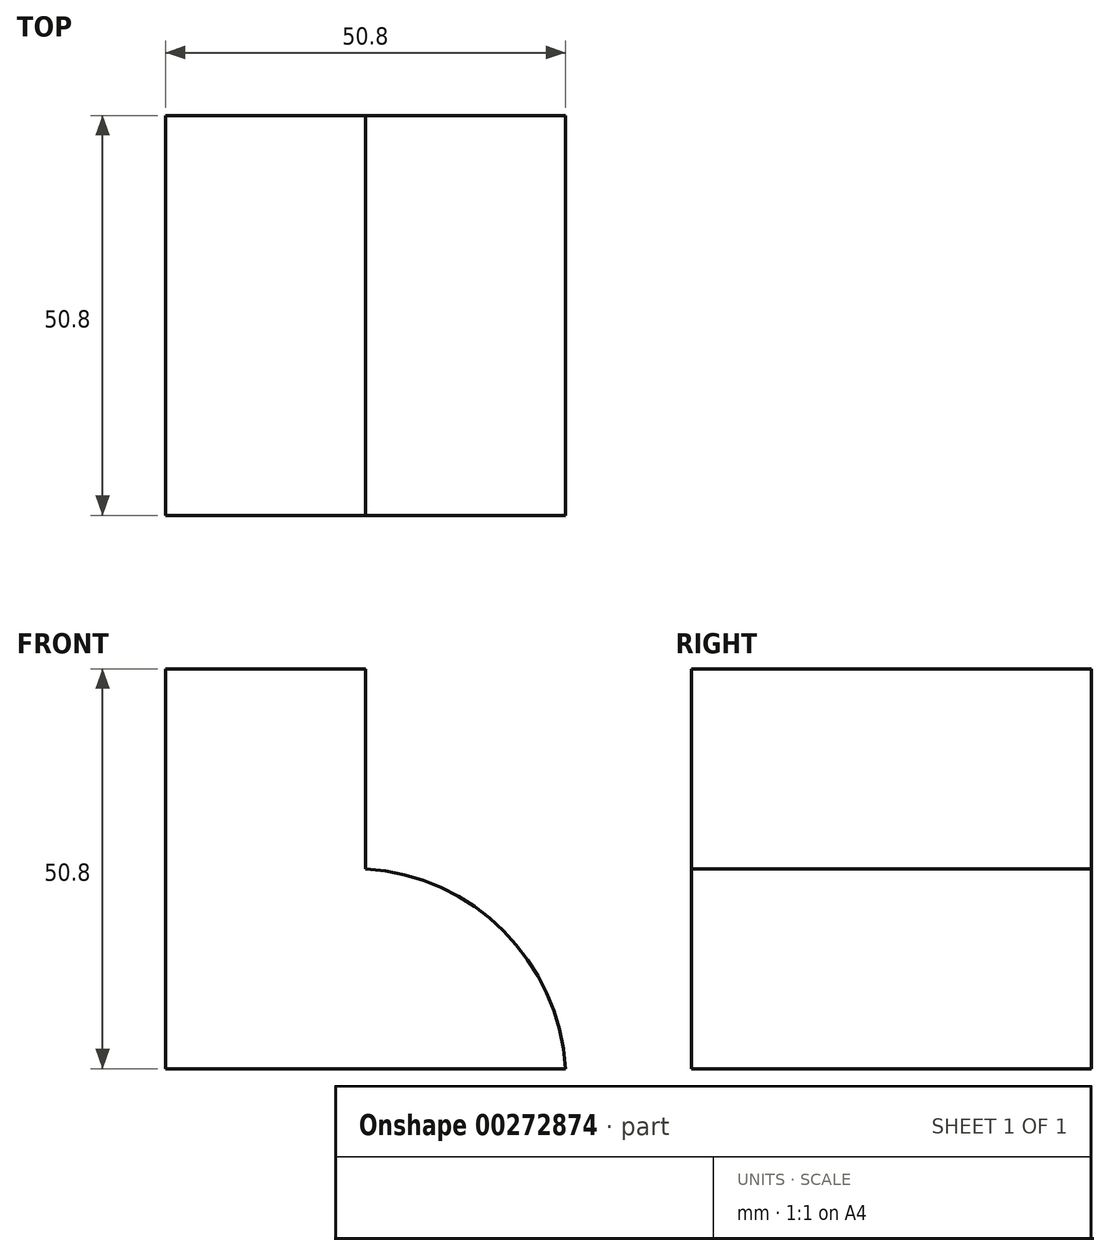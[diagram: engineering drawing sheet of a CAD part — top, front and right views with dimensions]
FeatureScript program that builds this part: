
annotation { "Feature Type Name" : "Feature", "Feature Type Description" : "" }
export const myFeature = defineFeature(function(context is Context, id is Id, definition is map)
    precondition{}
    {
        {
            var Q0;
            Q0=qCreatedBy(makeId("Front.planeOp"),FACE);
            var sketch = newSketch(context, id + "F0", { "sketchPlane" : qUnion([Q0])});
            skLineSegment(sketch, "E0", {"start": v(0, 0) * mm, "end": v(-50.8, 0) * mm});
            skLineSegment(sketch, "E1", {"start": v(-50.8, 0) * mm, "end": v(-50.8, 50.8) * mm});
            skLineSegment(sketch, "E2", {"start": v(-50.8, 50.8) * mm, "end": v(-25.4, 50.8) * mm});
            skLineSegment(sketch, "E3", {"start": v(-25.4, 50.8) * mm, "end": v(-25.4, 25.4) * mm});
            skArc(sketch, "E4", {"start": v(0, 0) * mm, "mid": v(-7.88, 17.52) * mm, "end": v(-25.4, 25.4) * mm});
            skSolve(sketch);
        }
        {
            var Q0;
            Q0 = qSketchRegion(id + "F0", true);
            extrude(context, id + "F1", {"entities" : qUnion([Q0]), "depth" : 50.8 * mm});
        }
    });
